FCSTD DOCUMENT  (FreeCAD 0.20R29177 (Git))
Label: CArriageAssembly
License: All rights reserved
LicenseURL: http://en.wikipedia.org/wiki/All_rights_reserved
objects: App::Link×12, App::DocumentObjectGroup×3, PartDesign::CoordinateSystem×3, App::FeaturePython×1, App::MeasureDistance×1, App::Part×1
note: 3 computed .brp shape members not serialized (recipe doc carries the construction recipe); baked Part::Feature solids carry a one-line shape summary decoded from their .brp
EXTERNAL_REF file=Plate1.FCStd obj=LCS_0
EXTERNAL_REF file=Plate1.FCStd obj=Body
EXTERNAL_REF file=PlateSide.FCStd obj=LCS_0
EXTERNAL_REF file=PlateSide.FCStd obj=Body
EXTERNAL_REF file=CBEAM.FCStd obj=LCS_22
EXTERNAL_REF file=CBEAM.FCStd obj=Model
EXTERNAL_REF file=PlateSide.FCStd obj=LCS_WheelBM
EXTERNAL_REF file=VWeel.FCStd obj=LCS_1_EDGE
EXTERNAL_REF file=VWeel.FCStd obj=Model
EXTERNAL_REF file=PlateSide.FCStd obj=LCS_WheelBL001
EXTERNAL_REF file=PlateSide.FCStd obj=LCS_WheelBL
EXTERNAL_REF file=PlateSide.FCStd obj=LCS_WheelTL
EXTERNAL_REF file=PlateSide.FCStd obj=LCS_WheelTR
EXTERNAL_REF file=PlateSide.FCStd obj=LCS_1
EXTERNAL_REF file=Backlash.FCStd obj=LCS_2
EXTERNAL_REF file=Backlash.FCStd obj=Baclash
EXTERNAL_REF file=Nema.FCStd obj=LCS_1
EXTERNAL_REF file=PlateSide.FCStd obj=LCS_2_Central
EXTERNAL_REF file=Nema.FCStd obj=Nema_23
EXTERNAL_REF file=CBEAM.FCStd obj=LCS_Origin
EXTERNAL_REF file=EndPlates.FCStd obj=LCS_1_LH
EXTERNAL_REF file=EndPlates.FCStd obj=Body

FEATURE [App::DocumentObjectGroup] Parts
FEATURE [PartDesign::CoordinateSystem] LCS_Origin
  AttacherType = Attacher::AttachEngine3D
  MapMode = 2
  Support = -> [X_Axis]
FEATURE [App::DocumentObjectGroup] Constraints
FEATURE [App::FeaturePython] Variables  # WARN: FeaturePython — macro-defined, semantics opaque (R4)
  Type = App::PropertyContainer
FEATURE [App::DocumentObjectGroup] Configurations
FEATURE [App::Link] Body
  AssemblyType = Part::Link
  AttachedBy = #LCS_0
  AttachedTo = Parent Assembly#LCS_Origin
  AttachmentOffset = pos=(0,0,48) rot=(0,0,1;0rad)
  LinkPlacement = pos=(0,0,48) rot=(0,0,1;0rad)
  LinkedObject = -> <external Plate1.FCStd>#Body
  Placement = pos=(0,0,48) rot=(0,0,1;0rad)
  SolverId = Asm4EE
  expr: Placement = LCS_Origin.Placement * AttachmentOffset * Plate1#LCS_0.Placement ^ -1
FEATURE [App::Link] Body001
  AssemblyType = Part::Link
  AttachedBy = #LCS_0
  AttachedTo = Body#LCS_0
  AttachmentOffset = pos=(0,0,74) rot=(0,0,1;0rad)
  LinkPlacement = pos=(0,0,122) rot=(0,0,1;0rad)
  LinkedObject = -> <external PlateSide.FCStd>#Body
  Placement = pos=(0,0,122) rot=(0,0,1;0rad)
  SolverId = Asm4EE
  expr: Placement = Body.Placement * Plate1#LCS_0.Placement * AttachmentOffset * PlateSide#LCS_0.Placement ^ -1
FEATURE [App::Link] CBEAM
  AttachedBy = #LCS_22
  AttachedTo = Body001#LCS_0
  AttachmentOffset = pos=(40,159.5,-989) rot=(0,1,0;3.14159rad)
  LinkPlacement = pos=(70,189.5,133) rot=(0.707107,0.707107,0;3.14159rad)
  LinkedObject = -> <external CBEAM.FCStd>#Model
  Placement = pos=(70,189.5,133) rot=(0.707107,0.707107,0;3.14159rad)
  SolverId = Asm4EE
  expr: Placement = Body001.Placement * PlateSide#LCS_0.Placement * AttachmentOffset * CBEAM#LCS_22.Placement ^ -1
FEATURE [App::Link] VWheel
  AttachedBy = #LCS_1_EDGE
  AttachedTo = Body001#LCS_WheelBM
  AttachmentOffset = pos=(0,0,-23) rot=(0,0,1;0rad)
  LinkPlacement = pos=(50,15,110.545) rot=(0,1,0;1.5708rad)
  LinkedObject = -> <external VWeel.FCStd>#Model
  Placement = pos=(50,15,110.545) rot=(0,1,0;1.5708rad)
  SolverId = Asm4EE
  expr: Placement = Body001.Placement * PlateSide#LCS_WheelBM.Placement * AttachmentOffset * VWeel#LCS_1_EDGE.Placement ^ -1
FEATURE [App::Link] VWheel001
  AttachedBy = #LCS_1_EDGE
  AttachedTo = Body001#LCS_WheelBL001
  AttachmentOffset = pos=(0,0,-23) rot=(0,0,1;0rad)
  LinkPlacement = pos=(85,15,110.545) rot=(0,1,0;1.5708rad)
  LinkedObject = -> <external VWeel.FCStd>#Model
  Placement = pos=(85,15,110.545) rot=(0,1,0;1.5708rad)
  SolverId = Asm4EE
  expr: Placement = Body001.Placement * PlateSide#LCS_WheelBL001.Placement * AttachmentOffset * VWeel#LCS_1_EDGE.Placement ^ -1
FEATURE [App::Link] VWheel002
  AttachedBy = #LCS_1_EDGE
  AttachedTo = Body001#LCS_WheelBL
  AttachmentOffset = pos=(0,0,-23) rot=(0,0,1;0rad)
  LinkPlacement = pos=(15,15,110.545) rot=(0,1,0;1.5708rad)
  LinkedObject = -> <external VWeel.FCStd>#Model
  Placement = pos=(15,15,110.545) rot=(0,1,0;1.5708rad)
  SolverId = Asm4EE
  expr: Placement = Body001.Placement * PlateSide#LCS_WheelBL.Placement * AttachmentOffset * VWeel#LCS_1_EDGE.Placement ^ -1
FEATURE [App::Link] VWheel003
  AttachedBy = #LCS_1_EDGE
  AttachedTo = Body001#LCS_WheelTL
  AttachmentOffset = pos=(0,0,-23) rot=(0,0,1;0rad)
  LinkPlacement = pos=(16.6299,115,110.545) rot=(0,1,0;1.5708rad)
  LinkedObject = -> <external VWeel.FCStd>#Model
  Placement = pos=(16.6299,115,110.545) rot=(0,1,0;1.5708rad)
  SolverId = Asm4EE
  expr: Placement = Body001.Placement * PlateSide#LCS_WheelTL.Placement * AttachmentOffset * VWeel#LCS_1_EDGE.Placement ^ -1
FEATURE [App::Link] VWheel004
  AttachedBy = #LCS_1_EDGE
  AttachedTo = Body001#LCS_WheelTR
  AttachmentOffset = pos=(0,0,-23) rot=(0,0,1;0rad)
  LinkPlacement = pos=(86.6299,115,110.545) rot=(0,1,0;1.5708rad)
  LinkedObject = -> <external VWeel.FCStd>#Model
  Placement = pos=(86.6299,115,110.545) rot=(0,1,0;1.5708rad)
  SolverId = Asm4EE
  expr: Placement = Body001.Placement * PlateSide#LCS_WheelTR.Placement * AttachmentOffset * VWeel#LCS_1_EDGE.Placement ^ -1
FEATURE [App::Link] CBEAM001
  AttachedBy = #LCS_22
  AttachedTo = Body001#LCS_1
  AttachmentOffset = pos=(400,75,-31.5) rot=(0,1,0;1.5708rad)
  LinkPlacement = pos=(-600,105,120.5) rot=(0.57735,0.57735,0.57735;2.0944rad)
  LinkedObject = -> <external CBEAM.FCStd>#Model
  Placement = pos=(-600,105,120.5) rot=(0.57735,0.57735,0.57735;2.0944rad)
  SolverId = Asm4EE
  expr: Placement = Body001.Placement * PlateSide#LCS_1.Placement * AttachmentOffset * CBEAM#LCS_22.Placement ^ -1
FEATURE [App::Link] Baclash
  AssemblyType = Part::Link
  AttachedBy = #LCS_2
  AttachedTo = Body001#LCS_WheelBM
  AttachmentOffset = pos=(60,7,-6) rot=(0,0,1;1.5708rad)
  LinkPlacement = pos=(33,65,116) rot=(0.57735,-0.57735,0.57735;4.18879rad)
  LinkedObject = -> <external Backlash.FCStd>#Baclash
  Placement = pos=(33,65,116) rot=(0.57735,-0.57735,0.57735;4.18879rad)
  SolverId = Asm4EE
  expr: Placement = Body001.Placement * PlateSide#LCS_WheelBM.Placement * AttachmentOffset * Backlash#LCS_2.Placement ^ -1
FEATURE [App::MeasureDistance] Distance  label="Distance: 100,04 mm"
  Distance = 100.039
  P1 = (0,160.852,128)
  P2 = (100,158.07,128)
FEATURE [App::Link] Nema_024  label="Nema 024"
  AssemblyType = Part::Link
  AttachedBy = #LCS_1
  AttachedTo = Body001#LCS_2_Central
  AttachmentOffset = pos=(0,0,31) rot=(1,0,0;3.14159rad)
  LinkPlacement = pos=(20.2533,204.569,275.354) rot=(1,0,0;3.14159rad)
  LinkedObject = -> <external Nema.FCStd>#Nema_23
  Placement = pos=(20.2533,204.569,275.354) rot=(1,0,0;3.14159rad)
  SolverId = Asm4EE
  expr: Placement = Body001.Placement * PlateSide#LCS_2_Central.Placement * AttachmentOffset * Nema#LCS_1.Placement ^ -1
FEATURE [PartDesign::CoordinateSystem] LCS_Shaft
  AttacherType = Attacher::AttachEngine3D
FEATURE [PartDesign::CoordinateSystem] LCS_1_Central
  AttacherType = Attacher::AttachEngine3D
FEATURE [App::Link] Body002
  AssemblyType = Part::Link
  AttachedBy = #LCS_1_LH
  AttachedTo = CBEAM001#LCS_Origin
  AttachmentOffset = pos=(-70,-10,0) rot=(0,0,1;0rad)
  LinkPlacement = pos=(-606,-16.8489,120.5) rot=(0,1,0;1.5708rad)
  LinkedObject = -> <external EndPlates.FCStd>#Body
  Placement = pos=(-606,-16.8489,120.5) rot=(0,1,0;1.5708rad)
  SolverId = Asm4EE
  expr: Placement = CBEAM001.Placement * CBEAM#LCS_Origin.Placement * AttachmentOffset * EndPlates#LCS_1_LH.Placement ^ -1
FEATURE [App::Part] Model
  AssemblyType = Part::Link
  Group = -> [LCS_Origin,Constraints,Variables,Configurations,Body,Body001,CBEAM,VWheel,VWheel001,VWheel002,VWheel003,VWheel004,CBEAM001,Baclash,Nema_024,LCS_Shaft,LCS_1_Central,Body002]
  Origin = -> Origin
  Type = Assembly

RESOLVED EXTERNAL PARTS (link-assembly join: the EXTERNAL_REF files above that resolve inside this repo's crawl, each included once):
---- part EndPlates.FCStd = doc fcstd_78b9f20a3a43 ----
FCSTD DOCUMENT  (FreeCAD 0.20R29177 (Git))
Label: EndPlates
License: All rights reserved
LicenseURL: http://en.wikipedia.org/wiki/All_rights_reserved
objects: Sketcher::SketchObject×2, PartDesign::Pad×1, PartDesign::CoordinateSystem×1, PartDesign::Body×1
note: 6 computed .brp shape members not serialized (recipe doc carries the construction recipe); baked Part::Feature solids carry a one-line shape summary decoded from their .brp

FEATURE [Sketcher::SketchObject] Sketch
  FullyConstrained = false
  MapMode = 5
  Support = -> [XY_Plane]
  sketch-geometry (14):
    g0: LineSegment StartX=181.481 StartY=0 StartZ=0 EndX=181.481 EndY=63.6335 EndZ=0
    g1: LineSegment StartX=181.481 StartY=63.6335 StartZ=0 EndX=100 EndY=180 EndZ=0
    g2: LineSegment StartX=100 StartY=180 StartZ=0 EndX=0 EndY=180 EndZ=0
    g3: LineSegment StartX=0 StartY=180 StartZ=0 EndX=0 EndY=100 EndZ=0
    g4: LineSegment StartX=0 StartY=100 StartZ=0 EndX=60 EndY=100 EndZ=0
    g5: LineSegment StartX=111.775 StartY=48.2248 StartZ=0 EndX=111.775 EndY=0 EndZ=0
    g6: ArcOfCircle CenterX=60 CenterY=48.2248 CenterZ=0 NormalX=0 NormalY=0 NormalZ=1 AngleXU=0 Radius=51.7752 StartAngle=0 EndAngle=1.5708
    g7: Circle CenterX=10 CenterY=170 CenterZ=0 NormalX=0 NormalY=0 NormalZ=1 AngleXU=0 Radius=2.5
    g8: Circle CenterX=30 CenterY=170 CenterZ=0 NormalX=0 NormalY=0 NormalZ=1 AngleXU=0 Radius=2.5
    g9: Circle CenterX=30 CenterY=150 CenterZ=0 NormalX=0 NormalY=0 NormalZ=1 AngleXU=0 Radius=2.5
    g10: Circle CenterX=30 CenterY=130 CenterZ=0 NormalX=0 NormalY=0 NormalZ=1 AngleXU=0 Radius=2.5
    g11: Circle CenterX=30 CenterY=110 CenterZ=0 NormalX=0 NormalY=0 NormalZ=1 AngleXU=0 Radius=2.5
    g12: Circle CenterX=10 CenterY=110 CenterZ=0 NormalX=0 NormalY=0 NormalZ=1 AngleXU=0 Radius=2.5
    g13: LineSegment StartX=111.775 StartY=0 StartZ=0 EndX=181.481 EndY=0 EndZ=0
  constraints (39):
    c: PointOnObject(g0,g-1)
    c: Vertical(g0)
    c: Coincident(g0,g1)
    c: Coincident(g1,g2)
    c: PointOnObject(g2,g-2)
    c: Horizontal(g2)
    c: Coincident(g2,g3)
    c: PointOnObject(g3,g-2)
    c: Coincident(g3,g4)
    c: Horizontal(g4)
    c: Angle(g1,g0) = 2.53073
    c: DistanceX(g2,g2) = 100
    c: DistanceY(g3,g3) = 80
    c: Vertical(g5)
    c: Tangent(g4,g6) = 1.5708
    c: Tangent(g5,g6) = 1.5708
    c: Diameter(g7) = 5
    c: Diameter(g12) = 5
    c: Diameter(g11) = 5
    c: Diameter(g10) = 5
    c: Diameter(g9) = 5
    c: Diameter(g8) = 5
    c: DistanceX(g2,g7) = 10
    c: DistanceX(g7,g8) = 20
    c: Vertical(g9,g8)
    c: Vertical(g10,g9)
    c: Vertical(g11,g10)
    c: Horizontal(g12,g11)
    c: Vertical(g12,g7)
    c: DistanceY(g11,g10) = 20
    c: DistanceY(g10,g9) = 20
    c: DistanceY(g9,g8) = 20
    c: Horizontal(g7,g8)
    c: DistanceY(g7,g2) = 10
    c: DistanceX(g4,g4) = 60
    c: DistanceY(g5,g1) = 180
    c: Coincident(g13,g5)
    c: Coincident(g13,g0)
    c: Horizontal(g13)
FEATURE [PartDesign::Pad] Pad
  Direction = (0,0,1)
  Length = 6
  Length2 = 10
  Profile = -> Sketch
  ReferenceAxis = -> Sketch [N_Axis]
  Type = 0
FEATURE [PartDesign::CoordinateSystem] LCS_1_LH
  AttacherType = Attacher::AttachEngine3D
  MapMode = 11
  Placement = pos=(30,170,6) rot=(0,0,1;1.5708rad)
  Support = -> [Pad]
FEATURE [Sketcher::SketchObject] Sketch001
  FullyConstrained = true
  MapMode = 5
  Support = -> [XY_Plane]
FEATURE [PartDesign::Body] Body
  Group = -> [Sketch,Pad,LCS_1_LH,Sketch001]
  Origin = -> Origin
  Tip = -> Pad
---- part Plate1.FCStd = doc fcstd_1cd25f8104a5 ----
FCSTD DOCUMENT  (FreeCAD 0.20R29177 (Git))
Label: Plate1
License: All rights reserved
LicenseURL: http://en.wikipedia.org/wiki/All_rights_reserved
objects: Path::FeaturePython×4, Part::FeaturePython×3, App::DocumentObjectGroup×3, Sketcher::SketchObject×2, PartDesign::CoordinateSystem×1, PartDesign::Pad×1, PartDesign::Pocket×1, App::FeaturePython×1, PartDesign::Fillet×1, PartDesign::Body×1, Path::FeatureCompoundPython×1
note: 15 computed .brp shape members not serialized (recipe doc carries the construction recipe); baked Part::Feature solids carry a one-line shape summary decoded from their .brp

FEATURE [PartDesign::CoordinateSystem] LCS_0
  AttacherType = Attacher::AttachEngine3D
  MapMode = 2
  Support = -> [X_Axis001]
FEATURE [Sketcher::SketchObject] Sketch_1
  FullyConstrained = false
  sketch-geometry (11):
    g0: LineSegment StartX=0 StartY=0 StartZ=0 EndX=100 EndY=0 EndZ=0
    g1: LineSegment StartX=100 StartY=0 StartZ=0 EndX=100 EndY=135 EndZ=0
    g2: LineSegment StartX=100 StartY=135 StartZ=0 EndX=0 EndY=135 EndZ=0
    g3: LineSegment StartX=0 StartY=135 StartZ=0 EndX=0 EndY=0 EndZ=0
    g4: Circle CenterX=15 CenterY=15 CenterZ=0 NormalX=0 NormalY=0 NormalZ=1 AngleXU=0 Radius=3.525
    g5: Circle CenterX=50 CenterY=15 CenterZ=0 NormalX=0 NormalY=0 NormalZ=1 AngleXU=0 Radius=3.525
    g6: Circle CenterX=85 CenterY=15 CenterZ=0 NormalX=0 NormalY=0 NormalZ=1 AngleXU=0 Radius=3.525
    g7: Circle CenterX=16.6299 CenterY=115 CenterZ=0 NormalX=0 NormalY=0 NormalZ=1 AngleXU=0 Radius=2.55
    g8: Circle CenterX=86.6299 CenterY=115 CenterZ=0 NormalX=0 NormalY=0 NormalZ=1 AngleXU=0 Radius=2.55
    g9: GeomPoint X=32.5 Y=15 Z=0
    g10: GeomPoint X=67.5 Y=15 Z=0
  constraints (26):
    c: Coincident(g0,g1)
    c: Coincident(g1,g2)
    c: Coincident(g2,g3)
    c: Coincident(g3,g0)
    c: Horizontal(g0)
    c: Horizontal(g2)
    c: Vertical(g1)
    c: Vertical(g3)
    c: Coincident(g0,g-1)
    c: Radius(g4) = 3.525
    c: Equal(g4,g5) = 2.5
    c: Horizontal(g6,g5)
    c: DistanceY(g0,g4) = 15
    c: DistanceX(g0,g4) = 15
    c: DistanceX(g6,g0) = 15
    c: Symmetric(g4,g6,g5)
    c: Horizontal(g7,g8)
    c: DistanceY(g5,g7) = 100
    c: Symmetric(g4,g5,g9)
    c: Symmetric(g5,g6,g10)
    c: DistanceY(g7,g2) = 20
    c: DistanceX(g7,g8) = 70
    c: DistanceX(g2,g2) = 100
    c: Radius(g6) = 3.525
    c: Radius(g7) = 2.55
    c: Radius(g8) = 2.55
FEATURE [PartDesign::Pad] Pad
  Direction = (1,1,1)
  Length = 6
  Length2 = 100
  Profile = -> Sketch_1
  Type = 0
FEATURE [Sketcher::SketchObject] Sketch
  ExternalGeometry = -> [Pad]
  FullyConstrained = false
  MapMode = 5
  Placement = pos=(0,0,6) rot=(0,0,1;0rad)
  Support = -> [Pad]
  sketch-geometry (6):
    g0: LineSegment StartX=29.9 StartY=137.616 StartZ=0 EndX=70.1 EndY=137.616 EndZ=0
    g1: LineSegment StartX=70.1 StartY=137.616 StartZ=0 EndX=70.1 EndY=109.116 EndZ=0
    g2: LineSegment StartX=70.1 StartY=109.116 StartZ=0 EndX=29.9 EndY=109.116 EndZ=0
    g3: LineSegment StartX=29.9 StartY=109.116 StartZ=0 EndX=29.9 EndY=137.616 EndZ=0
    g4: GeomPoint X=50 Y=135 Z=0
    g5: GeomPoint X=50 Y=109.116 Z=0
  constraints (13):
    c: Coincident(g0,g1)
    c: Coincident(g1,g2)
    c: Coincident(g2,g3)
    c: Coincident(g3,g0)
    c: Horizontal(g0)
    c: Horizontal(g2)
    c: Vertical(g1)
    c: Vertical(g3)
    c: DistanceX(g0,g0) = 40.2
    c: Symmetric(g-3,g-3,g4)
    c: DistanceY(g3,g3) = 28.5
    c: Symmetric(g2,g1,g5)
    c: Vertical(g4,g5)
FEATURE [PartDesign::Pocket] Pocket
  BaseFeature = -> Pad
  Direction = (1,1,1)
  Length = 6
  Length2 = 100
  Profile = -> Sketch
  Type = 0
FEATURE [App::FeaturePython] SetupSheet  # Path/CAM operation (typed FeaturePython)
  ClearanceHeightExpression = OpStockZMax+SetupSheet.ClearanceHeightOffset
  ClearanceHeightOffset = 5
  CoolantMode = 0
  CoolantModes = None | Flood | Mist
  FinalDepthExpression = OpFinalDepth
  HorizRapid = 0
  SafeHeightExpression = OpStockZMax+SetupSheet.SafeHeightOffset
  SafeHeightOffset = 3
  StartDepthExpression = OpStartDepth
  StepDownExpression = OpToolDiameter
  VertRapid = 0
FEATURE [Part::FeaturePython] ToolBit001  label="4mmEndmill"  # Path/CAM toolbit (typed FeaturePython)
  BitPropertyNames = Chipload | CuttingEdgeHeight | Diameter | Flutes | Length | Material | ShankDiameter
  BitShape = <path>
  Chipload = 0
  CuttingEdgeHeight = 40
  Diameter = 4
  File = <userpath>/Backups/Downloads/CBeamEndplate/Toolbits/Bit/4mmEndmill.fctb
  Flutes = 0
  Length = 50
  Material = 0
  ShankDiameter = 4
  ShapeName = endmill
FEATURE [Path::FeaturePython] TC__4mmEndmill  label="TC: 4mmEndmill"  # Path/CAM operation (typed FeaturePython)
  HorizFeed = 6.66667
  HorizRapid = 0
  SpindleDir = 0
  SpindleSpeed = 0
  Tool = -> ToolBit001
  ToolNumber = 12
  VertFeed = 0.333333
  VertRapid = 0
  expr: HorizRapid = SetupSheet.HorizRapid
  expr: VertRapid = SetupSheet.VertRapid
FEATURE [App::DocumentObjectGroup] Tools
  Group = -> [TC__4mmEndmill]
FEATURE [PartDesign::Fillet] Fillet
  Base = -> Pocket [Edge5,Edge31,Edge32,Edge8]
  BaseFeature = -> Pocket
  Radius = 5
  SupportTransform = false
  UseAllEdges = false
FEATURE [PartDesign::Body] Body
  Group = -> [LCS_0,Sketch_1,Pad,Sketch,Pocket,Fillet]
  Origin = -> Origin001
  Tip = -> Fillet
FEATURE [App::DocumentObjectGroup] Parts
  Group = -> [Body]
FEATURE [Part::FeaturePython] Clone  label="Model-Body"  # Draft clone (typed FeaturePython)
  AttacherType = Attacher::AttachEngine3D
  Fuse = false
  Objects = -> [Body]
  PathResource = Model
  Scale = (1,1,1)
FEATURE [App::DocumentObjectGroup] Model
  Group = -> [Clone]
FEATURE [Part::FeaturePython] Stock  # WARN: FeaturePython — macro-defined, semantics opaque (R4)
  Base = -> Model
  ExtXneg = 0
  ExtXpos = 0
  ExtYneg = 0
  ExtYpos = 0
  ExtZneg = 0
  ExtZpos = 0
  StockType = FromBase
FEATURE [Path::FeaturePython] Profile  # Path/CAM operation (typed FeaturePython)
  Active = true
  AreaParams:
    Tolerance = 1e-07
    FitArcs = True
    Simplify = False
    CleanDistance = 0.0
    Accuracy = 0.01
    Unit = 1.0
    MinArcPoints = 4
    MaxArcPoints = 100
    ClipperScale = 10000000.0
    Fill = 0
    Coplanar = 0
    Reorient = True
    Outline = False
    Explode = False
    OpenMode = 0
    Deflection = 0.01
    SubjectFill = 0
    ClipFill = 0
    Offset = -2.0
    ExtraPass = 0
    Stepover = 0.0
    LastStepover = 0.0
    JoinType = 0
    EndType = 0
    MiterLimit = 2.0
    RoundPrecision = 0.0
    PocketMode = 0
    ToolRadius = 1.0
    PocketExtraOffset = 0.0
    PocketStepover = 0.0
    PocketLastStepover = 0.0
    FromCenter = False
    Angle = 45.0
    AngleShift = 0.0
    Shift = 0.0
    Thicken = False
    SectionCount = -1
    Stepdown = 1.0
    SectionOffset = 0.0
    SectionTolerance = 1e-06
    SectionMode = 2
    Project = False
  AttemptInverseAngle = true
  Base = -> [Clone]
  ClearanceHeight = 11
  CoolantMode = 0
  CycleTime = 00:07:47
  Direction = 0
  EnableRotation = 0
  FinalDepth = -0.4
  HandleMultipleFeatures = 0
  InverseAngle = false
  JoinType = 0
  LimitDepthToFace = true
  MiterLimit = 0.1
  OffsetExtra = 0
  OpFinalDepth = 6
  OpStartDepth = 6.4
  OpStockZMax = 6
  OpStockZMin = 0
  OpToolDiameter = 4
  PathParams = {'orientation': 1, 'feedrate': 6.666666666666667, 'feedrate_v': 0.3333333333333333, 'verbose': True, 'resume_height': 9.0, 'retraction': 11.0, 'return_end': True, 'preamble': False, 'start': Vector (86.61287379050536, 114.45790851865407, 11.0)}
  ReverseDirection = false
  SafeHeight = 9
  Side = 1
  SplitArcs = false
  StartDepth = 6.3
  StartPoint = (0,0,0)
  StepDown = 0.4
  ToolController = -> TC__4mmEndmill
  UseComp = true
  UseStartPoint = false
  processCircles = false
  processHoles = false
  processPerimeter = true
  expr: ClearanceHeight = OpStockZMax + SetupSheet.ClearanceHeightOffset
  expr: FinalDepth = -0.4
  expr: SafeHeight = OpStockZMax + SetupSheet.SafeHeightOffset
  expr: StartDepth = 6.3
  expr: StepDown = 0.4
FEATURE [Path::FeaturePython] Adaptive  # Path/CAM operation (typed FeaturePython)
  Active = true
  Base = -> [Clone]
  ClearanceHeight = 11
  CoolantMode = 0
  CycleTime = 00:49:24
  ExtensionCorners = true
  ExtensionLengthDefault = 0
  FinalDepth = -0.4
  FinishDepth = 0
  FinishingProfile = true
  ForceInsideOut = true
  HelixAngle = 5
  HelixConeAngle = 0
  HelixDiameterLimit = 0
  KeepToolDownRatio = 3
  LiftDistance = 0
  OpFinalDepth = 6
  OpStartDepth = 8
  OpStockZMax = 6
  OpStockZMin = 0
  OpToolDiameter = 4
  OperationType = 1
  SafeHeight = 9
  Side = 0
  StartDepth = 6.3
  StepDown = 2
  StepOver = 60
  StockToLeave = 0
  StopProcessing = false
  Stopped = false
  Tolerance = 0.1
  ToolController = -> TC__4mmEndmill
  UseHelixArcs = false
  UseOutline = false
  expr: ClearanceHeight = OpStockZMax + SetupSheet.ClearanceHeightOffset
  expr: FinalDepth = -0.4
  expr: SafeHeight = OpStockZMax + SetupSheet.SafeHeightOffset
  expr: StartDepth = 6.3
  expr: StepDown = 2
FEATURE [Path::FeatureCompoundPython] Operations  # Path/CAM operation (typed FeaturePython)
  Group = -> [Profile,Adaptive]
  UsePlacements = false
FEATURE [Path::FeaturePython] Job  # Path/CAM operation (typed FeaturePython)
  CycleTime = 00:57:11
  Fixtures = G54
  GeometryTolerance = 0.01
  JobType = 0
  LastPostProcessDate = 2022-07-31 09:37:32.740612
  LastPostProcessOutput = <userpath>/Projects/WorkBeeModofied/Plate1.nc
  Model = -> Model
  Operations = -> Operations
  OrderOutputBy = 0
  PostProcessor = 8
  PostProcessorOutputFile = <userpath>/Projects/WorkBeeModofied/Plate1.nc
  SetupSheet = -> SetupSheet
  SplitOutput = false
  Stock = -> Stock
  Tools = -> Tools
note: 1 file-system path scrubbed to <path> (originals preserved in the JSON sidecar)
---- part PlateSide.FCStd = doc fcstd_a08677590b76 ----
FCSTD DOCUMENT  (FreeCAD 0.20R29177 (Git))
Label: PlateSide
License: All rights reserved
LicenseURL: http://en.wikipedia.org/wiki/All_rights_reserved
objects: PartDesign::CoordinateSystem×8, Sketcher::SketchObject×8, PartDesign::Pocket×6, Path::FeaturePython×5, Part::FeaturePython×3, App::DocumentObjectGroup×3, PartDesign::Pad×1, PartDesign::Fillet×1, App::FeaturePython×1, PartDesign::Body×1, Path::FeatureCompoundPython×1
note: 39 computed .brp shape members not serialized (recipe doc carries the construction recipe); baked Part::Feature solids carry a one-line shape summary decoded from their .brp

FEATURE [PartDesign::CoordinateSystem] LCS_0
  AttacherType = Attacher::AttachEngine3D
  MapMode = 2
  Support = -> [X_Axis001]
FEATURE [Sketcher::SketchObject] Sketch_1
  FullyConstrained = false
  sketch-geometry (11):
    g0: LineSegment StartX=0 StartY=0 StartZ=0 EndX=100 EndY=0 EndZ=0
    g1: LineSegment StartX=100 StartY=0 StartZ=0 EndX=100 EndY=190 EndZ=0
    g2: LineSegment StartX=100 StartY=190 StartZ=0 EndX=0 EndY=190 EndZ=0
    g3: LineSegment StartX=0 StartY=190 StartZ=0 EndX=0 EndY=0 EndZ=0
    g4: Circle CenterX=15 CenterY=15 CenterZ=0 NormalX=0 NormalY=0 NormalZ=1 AngleXU=0 Radius=3.525
    g5: Circle CenterX=50 CenterY=15 CenterZ=0 NormalX=0 NormalY=0 NormalZ=1 AngleXU=0 Radius=3.525
    g6: Circle CenterX=85 CenterY=15 CenterZ=0 NormalX=0 NormalY=0 NormalZ=1 AngleXU=0 Radius=3.535
    g7: Circle CenterX=16.6299 CenterY=115 CenterZ=0 NormalX=0 NormalY=0 NormalZ=1 AngleXU=0 Radius=2.5
    g8: Circle CenterX=86.6299 CenterY=115 CenterZ=0 NormalX=0 NormalY=0 NormalZ=1 AngleXU=0 Radius=2.5
    g9: GeomPoint X=32.5 Y=15 Z=0
    g10: GeomPoint X=67.5 Y=15 Z=0
  constraints (24):
    c: Coincident(g0,g1)
    c: Coincident(g1,g2)
    c: Coincident(g2,g3)
    c: Coincident(g3,g0)
    c: Horizontal(g0)
    c: Horizontal(g2)
    c: Vertical(g1)
    c: Vertical(g3)
    c: Coincident(g0,g-1)
    c: Radius(g4) = 3.525
    c: Equal(g4,g5) = 2.5
    c: Horizontal(g6,g5)
    c: DistanceY(g0,g4) = 15
    c: DistanceX(g0,g4) = 15
    c: DistanceX(g6,g0) = 15
    c: Symmetric(g4,g6,g5)
    c: Horizontal(g7,g8)
    c: DistanceY(g5,g7) = 100
    c: Symmetric(g4,g5,g9)
    c: Symmetric(g5,g6,g10)
    c: DistanceX(g7,g8) = 70
    c: DistanceX(g2,g2) = 100
    c: DistanceY(g1,g1) = 190
    c: Radius(g6) = 3.535
FEATURE [PartDesign::Pad] Pad
  Direction = (1,1,1)
  Length = 6
  Length2 = 100
  Profile = -> Sketch_1
  Type = 0
FEATURE [Sketcher::SketchObject] Sketch
  FullyConstrained = false
  MapMode = 5
  Placement = pos=(0,0,6) rot=(0,0,1;0rad)
  Support = -> [Pad]
  sketch-geometry (6):
    g0: Circle CenterX=39.9789 CenterY=119.513 CenterZ=0 NormalX=0 NormalY=0 NormalZ=1 AngleXU=0 Radius=2.5
    g1: Circle CenterX=60.0322 CenterY=119.416 CenterZ=0 NormalX=0 NormalY=0 NormalZ=1 AngleXU=0 Radius=2.5
    g2: Circle CenterX=39.9789 CenterY=139.513 CenterZ=0 NormalX=0 NormalY=0 NormalZ=1 AngleXU=0 Radius=2.32283
    g3: Circle CenterX=39.9789 CenterY=159.513 CenterZ=0 NormalX=0 NormalY=0 NormalZ=1 AngleXU=0 Radius=2.5
    g4: Circle CenterX=39.9789 CenterY=179.513 CenterZ=0 NormalX=0 NormalY=0 NormalZ=1 AngleXU=0 Radius=2.5
    g5: Circle CenterX=59.9789 CenterY=179.359 CenterZ=0 NormalX=0 NormalY=0 NormalZ=1 AngleXU=0 Radius=2.5
  constraints (12):
    c: Radius(g0) = 2.5
    c: Radius(g1) = 2.5
    c: Vertical(g0,g2)
    c: DistanceY(g0,g2) = 20
    c: Radius(g3) = 2.5
    c: Vertical(g3,g0)
    c: DistanceY(g0,g3) = 40
    c: Radius(g4) = 2.5
    c: Vertical(g0,g4)
    c: DistanceY(g0,g4) = 60
    c: Radius(g5) = 2.5
    c: DistanceX(g4,g5) = 20
FEATURE [PartDesign::Pocket] Pocket
  BaseFeature = -> Pad
  Direction = (1,1,1)
  Length = 6
  Length2 = 100
  Profile = -> Sketch
  Type = 0
FEATURE [Sketcher::SketchObject] Sketch001
  FullyConstrained = true
  MapMode = 5
  Placement = pos=(0,0,6) rot=(0,0,1;0rad)
  Support = -> [Pocket]
FEATURE [PartDesign::CoordinateSystem] LCS_1
  AttacherType = Attacher::AttachEngine3D
FEATURE [PartDesign::CoordinateSystem] LCS_WheelTL
  AttacherType = Attacher::AttachEngine3D
  MapMode = 11
  Placement = pos=(16.6299,115,6) rot=(0,0,1;1.5708rad)
  Support = -> [Pocket]
FEATURE [PartDesign::CoordinateSystem] LCS_WheelTR
  AttacherType = Attacher::AttachEngine3D
  MapMode = 11
  Placement = pos=(86.6299,115,6) rot=(0,0,1;1.5708rad)
  Support = -> [Pocket]
FEATURE [PartDesign::CoordinateSystem] LCS_WheelBL
  AttacherType = Attacher::AttachEngine3D
  MapMode = 11
  Placement = pos=(15,15,6) rot=(0,0,1;1.5708rad)
  Support = -> [Pocket]
FEATURE [PartDesign::CoordinateSystem] LCS_WheelBM
  AttacherType = Attacher::AttachEngine3D
  MapMode = 11
  Placement = pos=(50,15,6) rot=(0,0,1;1.5708rad)
  Support = -> [Pocket]
FEATURE [PartDesign::CoordinateSystem] LCS_WheelBL001
  AttacherType = Attacher::AttachEngine3D
  MapMode = 11
  Placement = pos=(85,15,6) rot=(0,0,1;1.5708rad)
  Support = -> [Pocket]
FEATURE [Sketcher::SketchObject] Sketch002
  FullyConstrained = false
  MapMode = 5
  Placement = pos=(0,0,0) rot=(1,0,0;3.14159rad)
  Support = -> [Pocket]
  sketch-geometry (2):
    g0: Circle CenterX=42.9876 CenterY=-54.9836 CenterZ=0 NormalX=0 NormalY=0 NormalZ=1 AngleXU=0 Radius=2.5
    g1: Circle CenterX=42.9783 CenterY=-74.9539 CenterZ=0 NormalX=0 NormalY=0 NormalZ=1 AngleXU=0 Radius=2.5
  constraints (2):
    c: Radius(g0) = 2.5
    c: Equal(g0,g1) = 2
FEATURE [PartDesign::Pocket] Pocket001
  BaseFeature = -> Pocket
  Direction = (1,1,1)
  Length = 6
  Length2 = 100
  Profile = -> Sketch002
  Type = 0
FEATURE [Sketcher::SketchObject] Sketch003
  FullyConstrained = true
  MapMode = 5
  Placement = pos=(0,0,6) rot=(0,0,1;0rad)
  Support = -> [Pocket001]
  sketch-geometry (3):
    g0: Circle CenterX=65.4998 CenterY=149.501 CenterZ=0 NormalX=0 NormalY=0 NormalZ=1 AngleXU=0 Radius=5
    g1: LineSegment StartX=69.9998 StartY=174.922 StartZ=0 EndX=69.9998 EndY=124.08 EndZ=0
    g2: GeomPoint X=69.9998 Y=149.501 Z=0
  constraints (8):
    c: Vertical(g1)
    c: Symmetric(g1,g1,g2)
    c: Horizontal(g0,g2)
    c: DistanceX(g1) = 69.9998
    c: DistanceY(g1) = 174.922
    c: DistanceY(g1) = 124.08
    c: DistanceX(g0,g2) = 4.5
    c: Radius(g0) = 5
FEATURE [PartDesign::Pocket] Pocket002
  BaseFeature = -> Pocket001
  Direction = (1,1,1)
  Length = 6
  Length2 = 100
  Profile = -> Sketch003
  Type = 0
FEATURE [PartDesign::CoordinateSystem] LCS_2_Central
  AttacherType = Attacher::AttachEngine3D
  MapMode = 11
  Placement = pos=(65.4998,149.501,6) rot=(0,0,1;1.5708rad)
  Support = -> [Pocket002]
FEATURE [Sketcher::SketchObject] Sketch004
  FullyConstrained = false
  MapMode = 5
  Placement = pos=(0,0,6) rot=(0,0,1;0rad)
  Support = -> [Pocket002]
  sketch-geometry (2):
    g0: Circle CenterX=89.0736 CenterY=173.068 CenterZ=0 NormalX=0 NormalY=0 NormalZ=1 AngleXU=0 Radius=2.6
    g1: Circle CenterX=89.07 CenterY=125.988 CenterZ=0 NormalX=0 NormalY=0 NormalZ=1 AngleXU=0 Radius=2.6
  constraints (2):
    c: Radius(g0) = 2.6
    c: Radius(g1) = 2.6
FEATURE [PartDesign::Pocket] Pocket003
  BaseFeature = -> Pocket002
  Direction = (1,1,1)
  Length = 6
  Length2 = 100
  Profile = -> Sketch004
  Type = 0
FEATURE [PartDesign::Fillet] Fillet
  Base = -> Pocket003 [Edge5,Edge8]
  BaseFeature = -> Pocket003
  Radius = 5
  SupportTransform = false
  UseAllEdges = false
FEATURE [Sketcher::SketchObject] Sketch005
  ExternalGeometry = -> [Fillet]
  FullyConstrained = true
  MapMode = 5
  Placement = pos=(0,0,6) rot=(0,0,1;0rad)
  Support = -> [Fillet]
  sketch-geometry (1):
    g0: Circle CenterX=65.4998 CenterY=149.501 CenterZ=0 NormalX=0 NormalY=0 NormalZ=1 AngleXU=0 Radius=8.25
  constraints (2):
    c: Coincident(g0,g-3)
    c: Radius(g0) = 8.25
FEATURE [PartDesign::Pocket] Pocket004
  BaseFeature = -> Fillet
  Direction = (1,1,1)
  Length = 6
  Length2 = 100
  Profile = -> Sketch005
  Type = 0
FEATURE [App::FeaturePython] SetupSheet  # Path/CAM operation (typed FeaturePython)
  ClearanceHeightExpression = OpStockZMax+SetupSheet.ClearanceHeightOffset
  ClearanceHeightOffset = 5
  CoolantMode = 0
  CoolantModes = None | Flood | Mist
  FinalDepthExpression = OpFinalDepth
  HorizRapid = 0
  SafeHeightExpression = OpStockZMax+SetupSheet.SafeHeightOffset
  SafeHeightOffset = 3
  StartDepthExpression = OpStartDepth
  StepDownExpression = OpToolDiameter
  VertRapid = 0
FEATURE [Part::FeaturePython] ToolBit001  label="4mmEndmill"  # Path/CAM toolbit (typed FeaturePython)
  BitPropertyNames = Chipload | CuttingEdgeHeight | Diameter | Flutes | Length | Material | ShankDiameter
  BitShape = <path>
  Chipload = 0
  CuttingEdgeHeight = 40
  Diameter = 4
  File = <userpath>/Backups/Downloads/CBeamEndplate/Toolbits/Bit/4mmEndmill.fctb
  Flutes = 0
  Length = 50
  Material = 0
  ShankDiameter = 4
  ShapeName = endmill
FEATURE [Path::FeaturePython] TC__4mmEndmill  label="TC: 4mmEndmill"  # Path/CAM operation (typed FeaturePython)
  HorizFeed = 10
  HorizRapid = 0
  SpindleDir = 0
  SpindleSpeed = 0
  Tool = -> ToolBit001
  ToolNumber = 12
  VertFeed = 1
  VertRapid = 0
  expr: HorizRapid = SetupSheet.HorizRapid
  expr: VertRapid = SetupSheet.VertRapid
FEATURE [App::DocumentObjectGroup] Tools
  Group = -> [TC__4mmEndmill]
FEATURE [Sketcher::SketchObject] Sketch006
  ExternalGeometry = -> [Pocket004]
  FullyConstrained = true
  MapMode = 5
  Placement = pos=(0,0,6) rot=(0,0,1;0rad)
  Support = -> [Pocket004]
  sketch-geometry (2):
    g0: Circle CenterX=65.4998 CenterY=162.501 CenterZ=0 NormalX=0 NormalY=0 NormalZ=1 AngleXU=0 Radius=2.5
    g1: Circle CenterX=65.4998 CenterY=136.501 CenterZ=0 NormalX=0 NormalY=0 NormalZ=1 AngleXU=0 Radius=2.5
  constraints (6):
    c: Radius(g0) = 2.5
    c: Radius(g1) = 2.5
    c: Vertical(g1,g-3)
    c: Vertical(g1,g0)
    c: DistanceY(g1,g-3) = 13
    c: DistanceY(g-3,g0) = 13
FEATURE [PartDesign::Pocket] Pocket005
  BaseFeature = -> Pocket004
  Direction = (1,1,1)
  Length = 6
  Length2 = 100
  Profile = -> Sketch006
  Type = 0
FEATURE [PartDesign::Body] Body
  Group = -> [LCS_0,Sketch_1,Pad,Sketch,Pocket,Sketch001,LCS_1,LCS_WheelTL,LCS_WheelTR,LCS_WheelBL,LCS_WheelBM,LCS_WheelBL001,Sketch002,Pocket001,Sketch003,Pocket002,LCS_2_Central,Sketch004,Pocket003,Fillet,Sketch005,Pocket004,Sketch006,Pocket005]
  Origin = -> Origin001
  Tip = -> Pocket005
FEATURE [App::DocumentObjectGroup] Parts
  Group = -> [Body]
FEATURE [Part::FeaturePython] Clone  label="Model-Body"  # Draft clone (typed FeaturePython)
  AttacherType = Attacher::AttachEngine3D
  Fuse = false
  Objects = -> [Body]
  PathResource = Model
  Scale = (1,1,1)
FEATURE [App::DocumentObjectGroup] Model
  Group = -> [Clone]
FEATURE [Part::FeaturePython] Stock  # WARN: FeaturePython — macro-defined, semantics opaque (R4)
  Base = -> Model
  ExtXneg = 1
  ExtXpos = 1
  ExtYneg = 1
  ExtYpos = 1
  ExtZneg = 1
  ExtZpos = 1
  Placement = pos=(-1e-15,0,0) rot=(0,0,1;0rad)
  StockType = FromBase
FEATURE [Path::FeaturePython] Adaptive  # Path/CAM operation (typed FeaturePython)
  Active = true
  Base = -> [Clone]
  ClearanceHeight = 12
  CoolantMode = 0
  CycleTime = 00:04:17
  ExtensionCorners = true
  ExtensionLengthDefault = 0
  FinalDepth = -0.5
  FinishDepth = 0
  FinishingProfile = true
  ForceInsideOut = false
  HelixAngle = 5
  HelixConeAngle = 0
  HelixDiameterLimit = 0
  KeepToolDownRatio = 3
  LiftDistance = 0
  OpFinalDepth = 6
  OpStartDepth = 7
  OpStockZMax = 7
  OpStockZMin = -1
  OpToolDiameter = 4
  OperationType = 0
  SafeHeight = 10
  Side = 1
  StartDepth = 6.5
  StepDown = 2
  StepOver = 40
  StockToLeave = 0
  StopProcessing = false
  Stopped = false
  Tolerance = 0.1
  ToolController = -> TC__4mmEndmill
  UseHelixArcs = false
  UseOutline = false
  expr: ClearanceHeight = OpStockZMax + SetupSheet.ClearanceHeightOffset
  expr: FinalDepth = -0.5
  expr: SafeHeight = OpStockZMax + SetupSheet.SafeHeightOffset
  expr: StartDepth = 6.5
  expr: StepDown = 2
FEATURE [Path::FeaturePython] Adaptive001  # Path/CAM operation (typed FeaturePython)
  Active = true
  Base = -> [Clone]
  ClearanceHeight = 12
  CoolantMode = 0
  CycleTime = 00:23:57
  ExtensionCorners = true
  ExtensionLengthDefault = 0
  FinalDepth = -0.5
  FinishDepth = 0
  FinishingProfile = true
  ForceInsideOut = true
  HelixAngle = 5
  HelixConeAngle = 0
  HelixDiameterLimit = 0
  KeepToolDownRatio = 3
  LiftDistance = 0
  OpFinalDepth = 6
  OpStartDepth = 7
  OpStockZMax = 7
  OpStockZMin = -1
  OpToolDiameter = 4
  OperationType = 1
  SafeHeight = 10
  Side = 0
  StartDepth = 5.6
  StepDown = 3
  StepOver = 60
  StockToLeave = 0
  StopProcessing = false
  Stopped = false
  Tolerance = 0.1
  ToolController = -> TC__4mmEndmill
  UseHelixArcs = false
  UseOutline = false
  expr: ClearanceHeight = OpStockZMax + SetupSheet.ClearanceHeightOffset
  expr: FinalDepth = -0.5
  expr: SafeHeight = OpStockZMax + SetupSheet.SafeHeightOffset
  expr: StartDepth = 5.6
  expr: StepDown = 3
FEATURE [Path::FeaturePython] Profile  # Path/CAM operation (typed FeaturePython)
  Active = true
  AreaParams:
    Tolerance = 1e-07
    FitArcs = True
    Simplify = False
    CleanDistance = 0.0
    Accuracy = 0.01
    Unit = 1.0
    MinArcPoints = 4
    MaxArcPoints = 100
    ClipperScale = 10000000.0
    Fill = 0
    Coplanar = 0
    Reorient = True
    Outline = False
    Explode = False
    OpenMode = 0
    Deflection = 0.01
    SubjectFill = 0
    ClipFill = 0
    Offset = -2.0
    ExtraPass = 0
    Stepover = 0.0
    LastStepover = 0.0
    JoinType = 0
    EndType = 0
    MiterLimit = 2.0
    RoundPrecision = 0.0
    PocketMode = 0
    ToolRadius = 1.0
    PocketExtraOffset = 0.0
    PocketStepover = 0.0
    PocketLastStepover = 0.0
    FromCenter = False
    Angle = 45.0
    AngleShift = 0.0
    Shift = 0.0
    Thicken = False
    SectionCount = -1
    Stepdown = 1.0
    SectionOffset = 0.0
    SectionTolerance = 1e-06
    SectionMode = 2
    Project = False
  AttemptInverseAngle = true
  Base = -> [Clone]
  ClearanceHeight = 12
  CoolantMode = 0
  CycleTime = 00:03:26
  Direction = 0
  EnableRotation = 0
  FinalDepth = -0.5
  HandleMultipleFeatures = 0
  InverseAngle = false
  JoinType = 0
  LimitDepthToFace = true
  MiterLimit = 0.1
  OffsetExtra = 0
  OpFinalDepth = 6
  OpStartDepth = 7
  OpStockZMax = 7
  OpStockZMin = -1
  OpToolDiameter = 4
  PathParams = {'orientation': 1, 'feedrate': 10.0, 'feedrate_v': 1.0, 'verbose': True, 'resume_height': 10.0, 'retraction': 12.0, 'return_end': True, 'preamble': False, 'start': Vector (89.06325464551938, 126.58054176594098, 12.0)}
  ReverseDirection = false
  SafeHeight = 10
  Side = 1
  SplitArcs = false
  StartDepth = 6.5
  StartPoint = (0,0,0)
  StepDown = 0.4
  ToolController = -> TC__4mmEndmill
  UseComp = true
  UseStartPoint = false
  processCircles = false
  processHoles = false
  processPerimeter = true
  expr: ClearanceHeight = OpStockZMax + SetupSheet.ClearanceHeightOffset
  expr: FinalDepth = -0.5
  expr: SafeHeight = OpStockZMax + SetupSheet.SafeHeightOffset
  expr: StartDepth = 6.5
  expr: StepDown = 0.4
FEATURE [Path::FeatureCompoundPython] Operations  # Path/CAM operation (typed FeaturePython)
  Group = -> [Adaptive,Profile,Adaptive001]
  UsePlacements = false
FEATURE [Path::FeaturePython] Job  # Path/CAM operation (typed FeaturePython)
  CycleTime = 00:31:40
  Fixtures = G54
  GeometryTolerance = 0.01
  JobType = 0
  LastPostProcessDate = 2022-08-08 18:24:15.112960
  LastPostProcessOutput = <userpath>/Desktop/Sideplate4.nc
  Model = -> Model
  Operations = -> Operations
  OrderOutputBy = 0
  PostProcessor = 8
  PostProcessorOutputFile = Sideplate.nc
  SetupSheet = -> SetupSheet
  SplitOutput = false
  Stock = -> Stock
  Tools = -> Tools
note: 1 file-system path scrubbed to <path> (originals preserved in the JSON sidecar)
